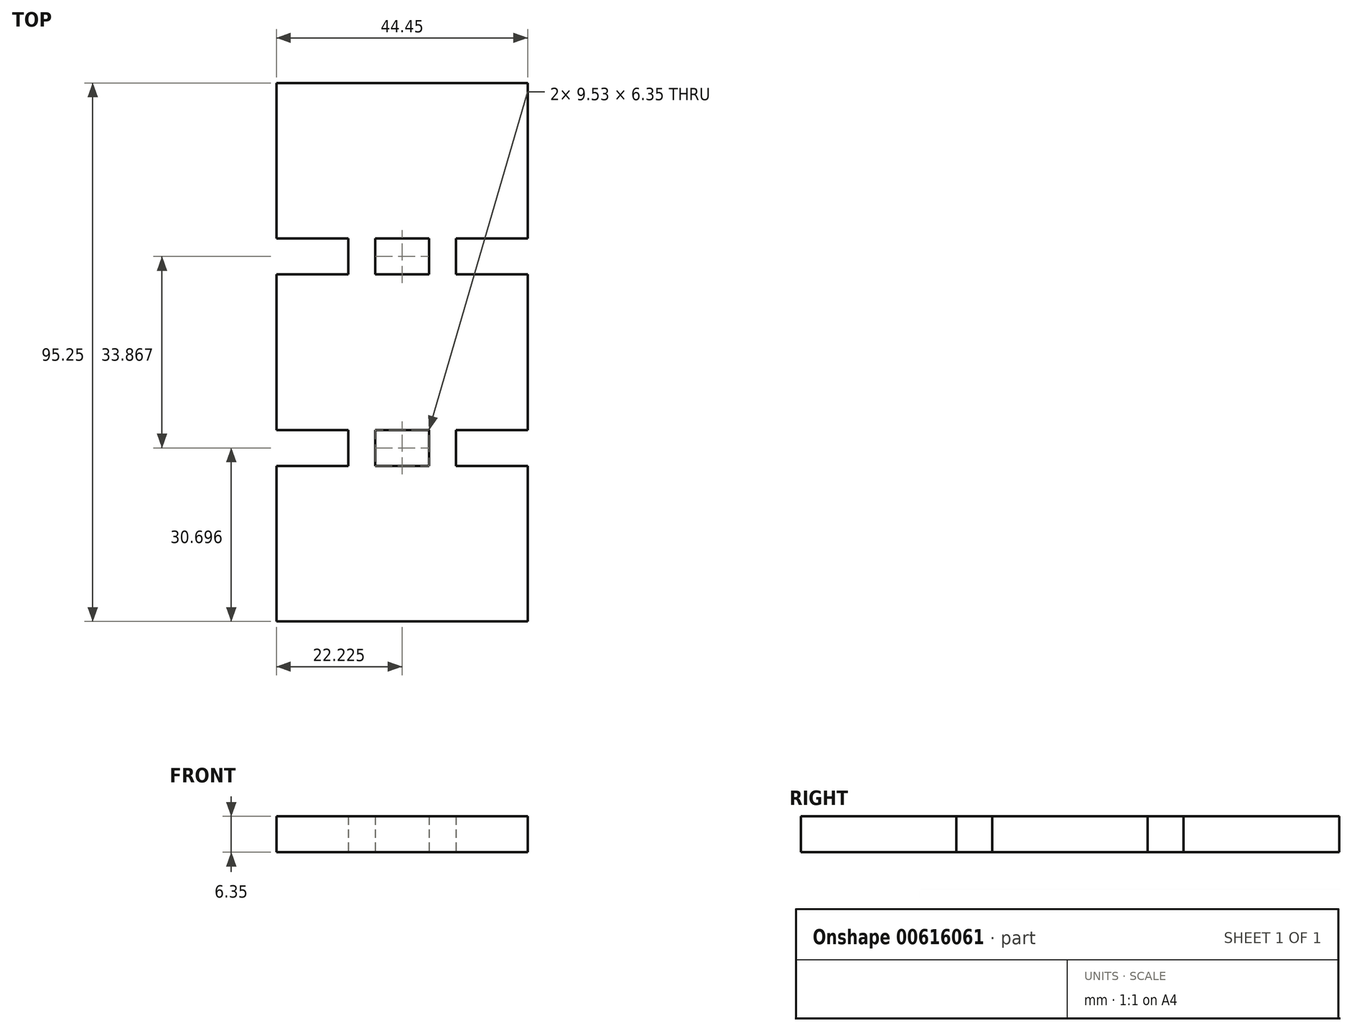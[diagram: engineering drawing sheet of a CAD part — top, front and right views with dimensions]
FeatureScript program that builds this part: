
annotation { "Feature Type Name" : "Feature", "Feature Type Description" : "" }
export const myFeature = defineFeature(function(context is Context, id is Id, definition is map)
    precondition{}
    {
        {
            var Q0;
            Q0=qCreatedBy(makeId("Top.planeOp"),FACE);
            var sketch = newSketch(context, id + "F0", { "sketchPlane" : qUnion([Q0])});
            skLineSegment(sketch, "E0.bottom", {"start": v(-25.4, -50.99) * mm, "end": v(19.05, -50.99) * mm});
            skLineSegment(sketch, "E0.top", {"start": v(-25.4, 44.26) * mm, "end": v(19.05, 44.26) * mm});
            skLineSegment(sketch, "E0.left", {"start": v(-25.4, -50.99) * mm, "end": v(-25.4, -23.47) * mm});
            skLineSegment(sketch, "E0.right", {"start": v(19.05, -50.99) * mm, "end": v(19.05, -23.47) * mm});
            skLineSegment(sketch, "E1.bottom", {"start": v(19.05, -17.12) * mm, "end": v(6.35, -17.12) * mm});
            skLineSegment(sketch, "E1.top", {"start": v(19.05, -23.47) * mm, "end": v(6.35, -23.47) * mm});
            skLineSegment(sketch, "E1.right", {"start": v(-12.7, -17.12) * mm, "end": v(-12.7, -23.47) * mm});
            skLineSegment(sketch, "E2.bottom", {"start": v(19.05, 16.75) * mm, "end": v(6.35, 16.75) * mm});
            skLineSegment(sketch, "E2.top", {"start": v(19.05, 10.4) * mm, "end": v(6.35, 10.4) * mm});
            skLineSegment(sketch, "E2.right", {"start": v(-12.7, 16.75) * mm, "end": v(-12.7, 10.4) * mm});
            skPoint(sketch, "E3.orphan", {"position": v(6.35, 16.75) * mm});
            skPoint(sketch, "E4.orphan", {"position": v(6.35, -23.47) * mm});
            skLineSegment(sketch, "E5.trimOffspring", {"start": v(19.05, 16.75) * mm, "end": v(19.05, 44.26) * mm});
            skLineSegment(sketch, "E6.trimOffspring", {"start": v(-25.4, 16.75) * mm, "end": v(-25.4, 44.26) * mm});
            skLineSegment(sketch, "E7.trimOffspring", {"start": v(19.05, -17.12) * mm, "end": v(19.05, 10.4) * mm});
            skLineSegment(sketch, "E8.trimOffspring", {"start": v(-25.4, -17.12) * mm, "end": v(-25.4, 10.4) * mm});
            skPoint(sketch, "E2.left.end.orphan", {"position": v(6.35, 10.4) * mm});
            skLineSegment(sketch, "E9", {"start": v(6.35, 16.75) * mm, "end": v(6.35, 10.4) * mm});
            skLineSegment(sketch, "E10.trimOffspring", {"start": v(-12.7, 16.75) * mm, "end": v(-25.4, 16.75) * mm});
            skLineSegment(sketch, "E11.trimOffspring", {"start": v(-12.7, 10.4) * mm, "end": v(-25.4, 10.4) * mm});
            skLineSegment(sketch, "E12.trimOffspring", {"start": v(-12.7, -17.12) * mm, "end": v(-25.4, -17.12) * mm});
            skLineSegment(sketch, "E13.trimOffspring", {"start": v(-12.7, -23.47) * mm, "end": v(-25.4, -23.47) * mm});
            skLineSegment(sketch, "E14", {"start": v(6.35, -17.12) * mm, "end": v(6.35, -23.47) * mm});
            skLineSegment(sketch, "E15.bottom", {"start": v(-7.94, -17.12) * mm, "end": v(1.59, -17.12) * mm});
            skLineSegment(sketch, "E15.top", {"start": v(-7.94, -23.47) * mm, "end": v(1.59, -23.47) * mm});
            skLineSegment(sketch, "E15.left", {"start": v(-7.94, -17.12) * mm, "end": v(-7.94, -23.47) * mm});
            skLineSegment(sketch, "E15.right", {"start": v(1.59, -17.12) * mm, "end": v(1.59, -23.47) * mm});
            skLineSegment(sketch, "E16", {"start": v(-25.4, -3.36) * mm, "end": v(19.05, -3.36) * mm, "construction": true});
            skLineSegment(sketch, "E17.MirrorCS", {"start": v(-7.94, 16.75) * mm, "end": v(1.59, 16.75) * mm});
            skLineSegment(sketch, "E18.MirrorCS", {"start": v(-7.94, 10.4) * mm, "end": v(1.59, 10.4) * mm});
            skLineSegment(sketch, "E19.MirrorCS", {"start": v(-7.94, 10.4) * mm, "end": v(-7.94, 16.75) * mm});
            skLineSegment(sketch, "E20.MirrorCS", {"start": v(1.59, 10.4) * mm, "end": v(1.59, 16.75) * mm});
            skSolve(sketch);
        }
        {
            var Q0;
            Q0 = qSketchRegion(id + "F0", true);
            extrude(context, id + "F1", {"entities" : qUnion([Q0]), "depth" : 6.35 * mm, "offsetDistance" : 25.4 * mm});
        }
    });
